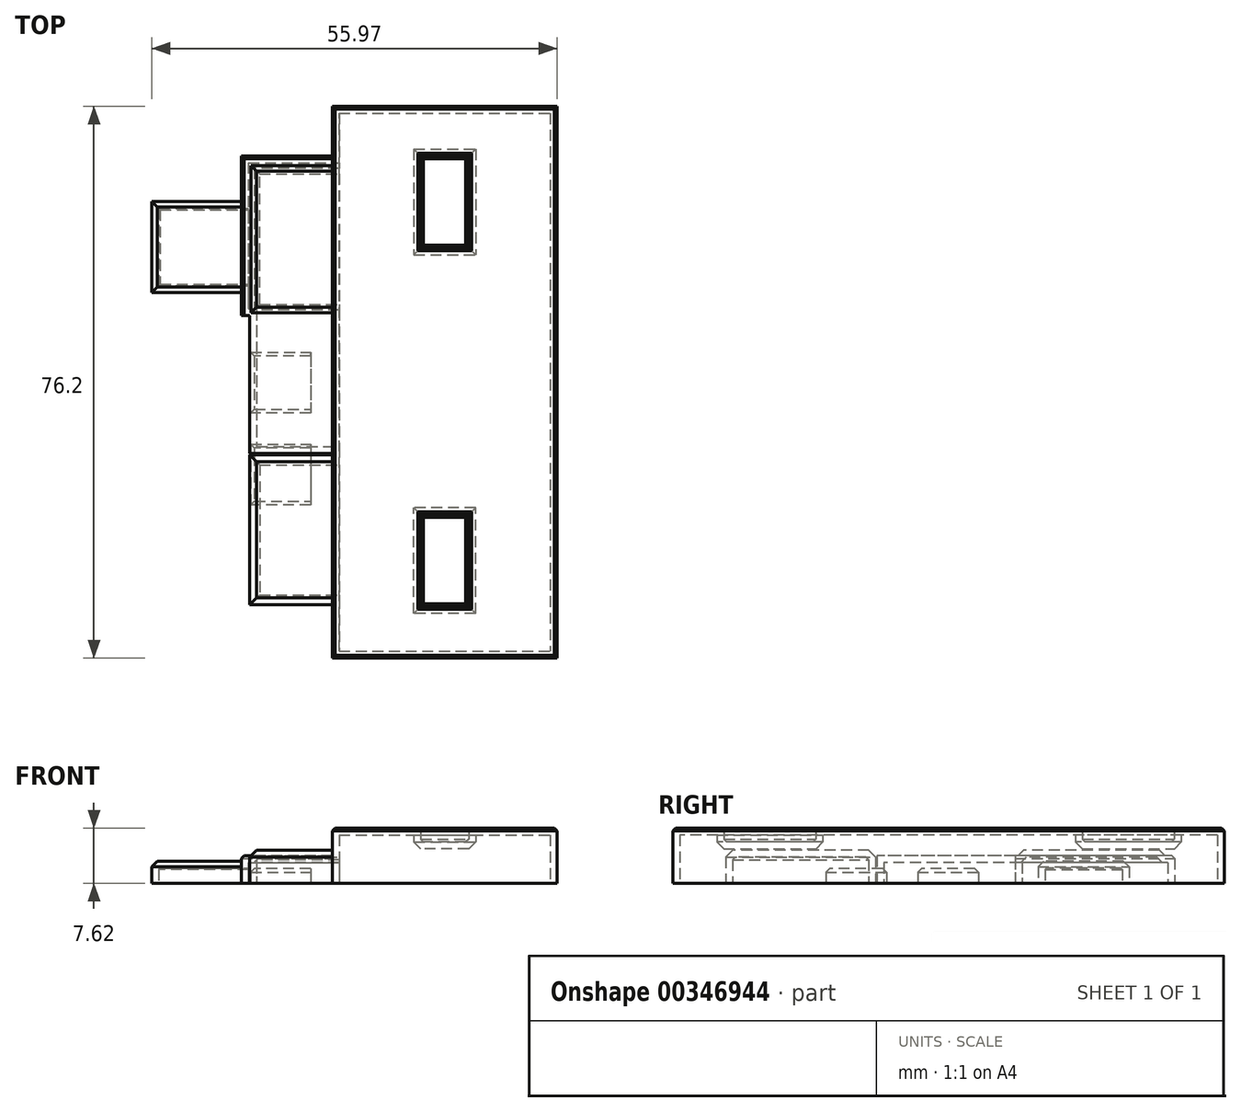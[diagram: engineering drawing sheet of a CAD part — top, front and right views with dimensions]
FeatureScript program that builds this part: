
annotation { "Feature Type Name" : "Feature", "Feature Type Description" : "" }
export const myFeature = defineFeature(function(context is Context, id is Id, definition is map)
    precondition{}
    {
        {
            var Q0;
            Q0=qCreatedBy(makeId("Top.planeOp"),FACE);
            var sketch = newSketch(context, id + "F0", { "sketchPlane" : qUnion([Q0])});
            skLineSegment(sketch, "E0.bottom", {"start": v(-10.71, 25.02) * mm, "end": v(9.98, 25.02) * mm});
            skLineSegment(sketch, "E0.top", {"start": v(-10.71, -25.78) * mm, "end": v(9.98, -25.78) * mm});
            skLineSegment(sketch, "E0.right", {"start": v(9.98, 25.02) * mm, "end": v(9.98, -25.78) * mm});
            skLineSegment(sketch, "E1.bottom", {"start": v(-27.33, 16.25) * mm, "end": v(-19.07, 16.25) * mm});
            skLineSegment(sketch, "E1.top", {"start": v(-27.33, 7.88) * mm, "end": v(-19.07, 7.88) * mm});
            skLineSegment(sketch, "E1.left", {"start": v(-27.33, 16.25) * mm, "end": v(-27.33, 7.88) * mm});
            skLineSegment(sketch, "E1.right", {"start": v(-19.07, 16.25) * mm, "end": v(-19.07, 7.88) * mm});
            skLineSegment(sketch, "E2.bottom", {"start": v(-2.56, 20.43) * mm, "end": v(1.85, 20.43) * mm});
            skLineSegment(sketch, "E2.top", {"start": v(-2.56, 11.96) * mm, "end": v(1.85, 11.96) * mm});
            skLineSegment(sketch, "E2.left", {"start": v(-2.56, 20.43) * mm, "end": v(-2.56, 11.96) * mm});
            skLineSegment(sketch, "E2.right", {"start": v(1.85, 20.43) * mm, "end": v(1.85, 11.96) * mm});
            skLineSegment(sketch, "E3.0.1.0", {"start": v(-2.56, -12.59) * mm, "end": v(1.85, -12.59) * mm});
            skLineSegment(sketch, "E3.0.1.1", {"start": v(-2.56, -12.59) * mm, "end": v(-2.56, -21.06) * mm});
            skLineSegment(sketch, "E3.0.1.2", {"start": v(1.85, -12.59) * mm, "end": v(1.85, -21.06) * mm});
            skLineSegment(sketch, "E3.0.1.3", {"start": v(-2.56, -21.06) * mm, "end": v(1.85, -21.06) * mm});
            skLineSegment(sketch, "E3.direction1", {"start": v(-2.56, 20.43) * mm, "end": v(4.81, 20.43) * mm, "construction": true});
            skLineSegment(sketch, "E3.direction2", {"start": v(-2.56, 20.43) * mm, "end": v(-2.56, -12.59) * mm, "construction": true});
            skLineSegment(sketch, "E4.0.1.0", {"start": v(-19.07, 3.55) * mm, "end": v(-19.07, -4.82) * mm});
            skLineSegment(sketch, "E4.0.1.1", {"start": v(-27.33, 3.55) * mm, "end": v(-19.07, 3.55) * mm});
            skLineSegment(sketch, "E4.0.1.2", {"start": v(-27.33, -4.82) * mm, "end": v(-19.07, -4.82) * mm});
            skLineSegment(sketch, "E4.0.1.3", {"start": v(-27.33, 3.55) * mm, "end": v(-27.33, -4.82) * mm});
            skLineSegment(sketch, "E4.0.2.0", {"start": v(-19.07, -9.15) * mm, "end": v(-19.07, -17.52) * mm});
            skLineSegment(sketch, "E4.0.2.1", {"start": v(-27.33, -9.15) * mm, "end": v(-19.07, -9.15) * mm});
            skLineSegment(sketch, "E4.0.2.2", {"start": v(-27.33, -17.52) * mm, "end": v(-19.07, -17.52) * mm});
            skLineSegment(sketch, "E4.0.2.3", {"start": v(-27.33, -9.15) * mm, "end": v(-27.33, -17.52) * mm});
            skLineSegment(sketch, "E5", {"start": v(-10.71, 25.02) * mm, "end": v(-10.71, -25.78) * mm});
            skLineSegment(sketch, "E6.bottom", {"start": v(-19.07, 20.46) * mm, "end": v(-10.71, 20.46) * mm});
            skLineSegment(sketch, "E6.top", {"start": v(-19.07, 5.76) * mm, "end": v(-10.71, 5.76) * mm});
            skLineSegment(sketch, "E6.left", {"start": v(-19.07, 20.46) * mm, "end": v(-19.07, 5.76) * mm});
            skLineSegment(sketch, "E6.right", {"start": v(-10.71, 20.46) * mm, "end": v(-10.71, 5.76) * mm});
            skLineSegment(sketch, "E7.top", {"start": v(-19.07, -6.96) * mm, "end": v(-10.71, -6.96) * mm});
            skLineSegment(sketch, "E7.left", {"start": v(-19.07, 5.76) * mm, "end": v(-19.07, -6.96) * mm});
            skLineSegment(sketch, "E7.right", {"start": v(-10.71, 5.76) * mm, "end": v(-10.71, -6.96) * mm});
            skLineSegment(sketch, "E8.top", {"start": v(-19.07, -21.65) * mm, "end": v(-10.71, -21.65) * mm});
            skLineSegment(sketch, "E8.left", {"start": v(-19.07, -6.96) * mm, "end": v(-19.07, -21.65) * mm});
            skLineSegment(sketch, "E8.right", {"start": v(-10.71, -6.96) * mm, "end": v(-10.71, -21.65) * mm});
            skLineSegment(sketch, "E9.0", {"start": v(-18.3, 19.7) * mm, "end": v(-10.71, 19.7) * mm});
            skLineSegment(sketch, "E9.2", {"start": v(-18.3, 5.9) * mm, "end": v(-10.71, 5.9) * mm});
            skLineSegment(sketch, "E10.0", {"start": v(-18.3, 5.76) * mm, "end": v(-10.71, 5.76) * mm});
            skLineSegment(sketch, "E10.2", {"start": v(-18.3, -6.96) * mm, "end": v(-10.71, -6.96) * mm});
            skLineSegment(sketch, "E11.MirrorCS", {"start": v(-19.07, -6.96) * mm, "end": v(-19.07, 7.73) * mm});
            skLineSegment(sketch, "E12.0", {"start": v(-18.3, -7.09) * mm, "end": v(-10.71, -7.09) * mm});
            skLineSegment(sketch, "E12.2", {"start": v(-18.3, -20.9) * mm, "end": v(-10.71, -20.9) * mm});
            skLineSegment(sketch, "E13", {"start": v(-18.3, 5.76) * mm, "end": v(-18.3, -6.96) * mm});
            skLineSegment(sketch, "E14", {"start": v(-18.3, -7.09) * mm, "end": v(-18.3, -20.9) * mm});
            skLineSegment(sketch, "E15", {"start": v(-18.3, 5.9) * mm, "end": v(-18.3, 19.7) * mm});
            skSolve(sketch);
        }
        {
            var Q0;
            {var subQ0=sQuery(id+"F0.wireOp",EDGE,"E0.bottom");Q0=makeQuery(id+"F0.imprint","IMPRINT",FACE,{"disambiguationData":[TD([[makeQuery(id+"F0.imprint","IMPRINT",EDGE,{"derivedFrom":subQ0}),-1.0]])]});}
            extrude(context, id + "F1", {"entities" : qUnion([Q0]), "depth" : 5.08 * mm});
        }
        {
            var Q0;
            {var subQ4=sQuery(id+"F0.wireOp",EDGE,"E6.bottom");Q0=makeQuery(id+"F0.imprint","IMPRINT",FACE,{"disambiguationData":[TD([[makeQuery(id+"F0.imprint","IMPRINT",EDGE,{"derivedFrom":subQ4}),-1.0]])]});}
            var Q1;
            {var subQ4=sQuery(id+"F0.wireOp",EDGE,"E6.top");Q1=makeQuery(id+"F0.imprint","IMPRINT",FACE,{"disambiguationData":[TD([[makeQuery(id+"F0.imprint","IMPRINT",EDGE,{"derivedFrom":subQ4}),-1.0]])]});}
            var Q2;
            {var subQ3=sQuery(id+"F0.wireOp",EDGE,"E7.top");Q2=makeQuery(id+"F0.imprint","IMPRINT",FACE,{"disambiguationData":[TD([[makeQuery(id+"F0.imprint","IMPRINT",EDGE,{"derivedFrom":subQ3}),-1.0]])]});}
            extrude(context, id + "F2", {"entities" : qUnion([Q0, Q1, Q2]), "operationType" : NewBodyOperationType.ADD, "depth" : 2.54 * mm});
        }
        {
            var Q0;
            {var subQ0=sQuery(id+"F0.wireOp",EDGE,"E1.bottom");Q0=makeQuery(id+"F0.imprint","IMPRINT",FACE,{"disambiguationData":[TD([[makeQuery(id+"F0.imprint","IMPRINT",EDGE,{"derivedFrom":subQ0}),-1.0]])]});}
            var Q1;
            {var subQ0=sQuery(id+"F0.wireOp",EDGE,"E4.0.1.1");Q1=makeQuery(id+"F0.imprint","IMPRINT",FACE,{"disambiguationData":[TD([[makeQuery(id+"F0.imprint","IMPRINT",EDGE,{"derivedFrom":subQ0}),-1.0]])]});}
            var Q2;
            {var subQ0=sQuery(id+"F0.wireOp",EDGE,"E4.0.2.1");Q2=makeQuery(id+"F0.imprint","IMPRINT",FACE,{"disambiguationData":[TD([[makeQuery(id+"F0.imprint","IMPRINT",EDGE,{"derivedFrom":subQ0}),-1.0]])]});}
            extrude(context, id + "F3", {"entities" : qUnion([Q0, Q1, Q2]), "operationType" : NewBodyOperationType.ADD, "depth" : 2.03 * mm});
        }
        {
            var Q0;
            {var subQ0=sQuery(id+"F0.wireOp",EDGE,"E9.0");Q0=makeQuery(id+"F0.imprint","IMPRINT",FACE,{"disambiguationData":[TD([[makeQuery(id+"F0.imprint","IMPRINT",EDGE,{"derivedFrom":subQ0}),-1.0]])]});}
            var Q1;
            {var subQ0=sQuery(id+"F0.wireOp",EDGE,"E10.0");Q1=makeQuery(id+"F0.imprint","IMPRINT",FACE,{"disambiguationData":[TD([[makeQuery(id+"F0.imprint","IMPRINT",EDGE,{"derivedFrom":subQ0}),-1.0]])]});}
            var Q2;
            {var subQ0=sQuery(id+"F0.wireOp",EDGE,"E12.0");Q2=makeQuery(id+"F0.imprint","IMPRINT",FACE,{"disambiguationData":[TD([[makeQuery(id+"F0.imprint","IMPRINT",EDGE,{"derivedFrom":subQ0}),-1.0]])]});}
            extrude(context, id + "F4", {"entities" : qUnion([Q0, Q1, Q2]), "operationType" : NewBodyOperationType.ADD, "depth" : 3.05 * mm});
        }
        {
            var Q0;
            Q0=makeQuery(id+"F0.imprint","IMPRINT",FACE,{"disambiguationData":[TD([[makeQuery(id+"F0.imprint","IMPRINT",EDGE,{"derivedFrom":sQuery(id+"F0.wireOp",EDGE,"E2.bottom")}),-1.0]])]});
            var Q1;
            Q1=makeQuery(id+"F0.imprint","IMPRINT",FACE,{"disambiguationData":[TD([[makeQuery(id+"F0.imprint","IMPRINT",EDGE,{"derivedFrom":sQuery(id+"F0.wireOp",EDGE,"E3.0.1.0")}),-1.0]])]});
            extrude(context, id + "F5", {"entities" : qUnion([Q0, Q1]), "operationType" : NewBodyOperationType.ADD, "depth" : 3.8 * mm});
        }
        {
            var Q0;
            Q0=makeQuery(id+"F4.opExtrude","CAP_EDGE",EDGE,{"disambiguationData":[OSD([sQuery(id+"F0.wireOp",EDGE,"E9.1")])],"isStart":false});
            var Q1;
            Q1=makeQuery(id+"F4.opExtrude","CAP_EDGE",EDGE,{"disambiguationData":[OSD([sQuery(id+"F0.wireOp",EDGE,"E10.1")])],"isStart":false});
            var Q2;
            Q2=makeQuery(id+"F4.opExtrude","CAP_EDGE",EDGE,{"disambiguationData":[OSD([sQuery(id+"F0.wireOp",EDGE,"E12.1")])],"isStart":false});
            var Q3;
            Q3=makeQuery(id+"F4.opExtrude","CAP_EDGE",EDGE,{"disambiguationData":[OSD([sQuery(id+"F0.wireOp",EDGE,"E12.2")])],"isStart":false});
            var Q4;
            Q4=makeQuery(id+"F4.opExtrude","CAP_EDGE",EDGE,{"disambiguationData":[OSD([sQuery(id+"F0.wireOp",EDGE,"E10.2")])],"isStart":false});
            var Q5;
            Q5=makeQuery(id+"F4.opExtrude","CAP_EDGE",EDGE,{"disambiguationData":[OSD([sQuery(id+"F0.wireOp",EDGE,"E9.2")])],"isStart":false});
            var Q6;
            Q6=makeQuery(id+"F4.opExtrude","CAP_EDGE",EDGE,{"disambiguationData":[OSD([sQuery(id+"F0.wireOp",EDGE,"E9.0")])],"isStart":false});
            var Q7;
            Q7=makeQuery(id+"F4.opExtrude","CAP_EDGE",EDGE,{"disambiguationData":[OSD([sQuery(id+"F0.wireOp",EDGE,"E10.0")])],"isStart":false});
            var Q8;
            Q8=makeQuery(id+"F4.opExtrude","CAP_EDGE",EDGE,{"disambiguationData":[OSD([sQuery(id+"F0.wireOp",EDGE,"E12.0")])],"isStart":false});
            var Q9;
            Q9=makeQuery(id+"F4.opExtrude","CAP_EDGE",EDGE,{"disambiguationData":[OSD([sQuery(id+"F0.wireOp",EDGE,"E13")])],"isStart":false});
            var Q10;
            Q10=makeQuery(id+"F4.opExtrude","CAP_EDGE",EDGE,{"disambiguationData":[OSD([sQuery(id+"F0.wireOp",EDGE,"E15")])],"isStart":false});
            var Q11;
            Q11=makeQuery(id+"F4.opExtrude","CAP_EDGE",EDGE,{"disambiguationData":[OSD([sQuery(id+"F0.wireOp",EDGE,"E14")])],"isStart":false});
            chamfer(context, id + "F6", {"entities" : qUnion([Q0, Q1, Q2, Q3, Q4, Q5, Q6, Q7, Q8, Q9, Q10, Q11]), "width" : 0.64 * mm, "tangentPropagation" : true});
        }
        {
            var Q0;
            Q0=makeQuery(id+"F1.opExtrude","CAP_FACE",FACE,{"disambiguationData":[OSD([sQuery(id+"F0.wireOp",EDGE,"E0.bottom"),sQuery(id+"F0.wireOp",EDGE,"E0.top"),sQuery(id+"F0.wireOp",EDGE,"E0.right"),sQuery(id+"F0.wireOp",EDGE,"E2.bottom"),sQuery(id+"F0.wireOp",EDGE,"E2.top"),sQuery(id+"F0.wireOp",EDGE,"E2.left"),sQuery(id+"F0.wireOp",EDGE,"E2.right"),sQuery(id+"F0.wireOp",EDGE,"E3.0.1.0"),sQuery(id+"F0.wireOp",EDGE,"E3.0.1.1"),sQuery(id+"F0.wireOp",EDGE,"E3.0.1.2"),sQuery(id+"F0.wireOp",EDGE,"E3.0.1.3"),sQuery(id+"F0.wireOp",EDGE,"E5"),sQuery(id+"F0.wireOp",EDGE,"E6.right"),sQuery(id+"F0.wireOp",EDGE,"E7.right"),sQuery(id+"F0.wireOp",EDGE,"E8.right")])],"isStart":false});
            chamfer(context, id + "F7", {"entities" : qUnion([Q0]), "width" : 0.25 * mm, "tangentPropagation" : true});
        }
        {
            var Q0;
            Q0=makeQuery(id+"F5.opExtrude","CAP_FACE",FACE,{"disambiguationData":[OSD([sQuery(id+"F0.wireOp",EDGE,"E2.bottom"),sQuery(id+"F0.wireOp",EDGE,"E2.top"),sQuery(id+"F0.wireOp",EDGE,"E2.left"),sQuery(id+"F0.wireOp",EDGE,"E2.right")])],"isStart":false});
            var Q1;
            Q1=makeQuery(id+"F5.opExtrude","CAP_FACE",FACE,{"disambiguationData":[OSD([sQuery(id+"F0.wireOp",EDGE,"E3.0.1.0"),sQuery(id+"F0.wireOp",EDGE,"E3.0.1.1"),sQuery(id+"F0.wireOp",EDGE,"E3.0.1.2"),sQuery(id+"F0.wireOp",EDGE,"E3.0.1.3")])],"isStart":false});
            chamfer(context, id + "F8", {"entities" : qUnion([Q0, Q1]), "width" : 0.25 * mm, "tangentPropagation" : true});
        }
        {
            var Q0;
            Q0=makeQuery(id+"F2.opExtrude","CAP_EDGE",EDGE,{"disambiguationData":[OSD([sQuery(id+"F0.wireOp",EDGE,"E6.left"),sQuery(id+"F0.wireOp",EDGE,"E8.left"),sQuery(id+"F0.wireOp",EDGE,"E11.MirrorCS")])],"isStart":false});
            var Q1;
            Q1=makeQuery(id+"F2.opExtrude","CAP_EDGE",EDGE,{"disambiguationData":[OSD([sQuery(id+"F0.wireOp",EDGE,"E6.bottom")])],"isStart":false});
            var Q2;
            Q2=makeQuery(id+"F2.opExtrude","CAP_EDGE",EDGE,{"disambiguationData":[OSD([sQuery(id+"F0.wireOp",EDGE,"E8.top")])],"isStart":false});
            chamfer(context, id + "F9", {"entities" : qUnion([Q0, Q1, Q2]), "width" : 0.25 * mm, "tangentPropagation" : true});
        }
        {
            var Q0;
            Q0=makeQuery(id+"F3.opExtrude","CAP_EDGE",EDGE,{"disambiguationData":[OSD([sQuery(id+"F0.wireOp",EDGE,"E1.left")])],"isStart":false});
            var Q1;
            Q1=makeQuery(id+"F3.opExtrude","CAP_EDGE",EDGE,{"disambiguationData":[OSD([sQuery(id+"F0.wireOp",EDGE,"E1.top")])],"isStart":false});
            var Q2;
            Q2=makeQuery(id+"F3.opExtrude","CAP_EDGE",EDGE,{"disambiguationData":[OSD([sQuery(id+"F0.wireOp",EDGE,"E1.bottom")])],"isStart":false});
            var Q3;
            Q3=makeQuery(id+"F3.opExtrude","CAP_EDGE",EDGE,{"disambiguationData":[OSD([sQuery(id+"F0.wireOp",EDGE,"E4.0.1.1")])],"isStart":false});
            var Q4;
            Q4=makeQuery(id+"F3.opExtrude","CAP_EDGE",EDGE,{"disambiguationData":[OSD([sQuery(id+"F0.wireOp",EDGE,"E4.0.1.3")])],"isStart":false});
            var Q5;
            Q5=makeQuery(id+"F3.opExtrude","CAP_EDGE",EDGE,{"disambiguationData":[OSD([sQuery(id+"F0.wireOp",EDGE,"E4.0.1.2")])],"isStart":false});
            var Q6;
            Q6=makeQuery(id+"F3.opExtrude","CAP_EDGE",EDGE,{"disambiguationData":[OSD([sQuery(id+"F0.wireOp",EDGE,"E4.0.2.1")])],"isStart":false});
            var Q7;
            Q7=makeQuery(id+"F3.opExtrude","CAP_EDGE",EDGE,{"disambiguationData":[OSD([sQuery(id+"F0.wireOp",EDGE,"E4.0.2.3")])],"isStart":false});
            var Q8;
            Q8=makeQuery(id+"F3.opExtrude","CAP_EDGE",EDGE,{"disambiguationData":[OSD([sQuery(id+"F0.wireOp",EDGE,"E4.0.2.2")])],"isStart":false});
            chamfer(context, id + "F10", {"entities" : qUnion([Q0, Q1, Q2, Q3, Q4, Q5, Q6, Q7, Q8]), "width" : 0.5 * mm, "tangentPropagation" : true});
        }
        {
            var Q0;
            {var subQ0=sQuery(id+"F0.wireOp",EDGE,"E3.0.1.3");var subQ1=sQuery(id+"F0.wireOp",EDGE,"E3.0.1.2");var subQ2=sQuery(id+"F0.wireOp",EDGE,"E3.0.1.1");var subQ3=sQuery(id+"F0.wireOp",EDGE,"E3.0.1.0");var subQ4=sQuery(id+"F0.wireOp",EDGE,"E2.right");var subQ5=sQuery(id+"F0.wireOp",EDGE,"E2.left");var subQ6=sQuery(id+"F0.wireOp",EDGE,"E2.top");var subQ7=sQuery(id+"F0.wireOp",EDGE,"E2.bottom");var subQ8=sQuery(id+"F0.wireOp",EDGE,"E7.right");var subQ9=sQuery(id+"F0.wireOp",EDGE,"E13");var subQ10=sQuery(id+"F0.wireOp",EDGE,"E10.2");var subQ11=sQuery(id+"F0.wireOp",EDGE,"E10.0");var subQ12=sQuery(id+"F0.wireOp",EDGE,"E14");var subQ13=sQuery(id+"F0.wireOp",EDGE,"E12.2");var subQ14=sQuery(id+"F0.wireOp",EDGE,"E12.0");var subQ15=sQuery(id+"F0.wireOp",EDGE,"E8.right");var subQ16=sQuery(id+"F0.wireOp",EDGE,"E15");var subQ17=sQuery(id+"F0.wireOp",EDGE,"E9.2");var subQ18=sQuery(id+"F0.wireOp",EDGE,"E9.0");var subQ19=sQuery(id+"F0.wireOp",EDGE,"E6.right");var subQ20=sQuery(id+"F0.wireOp",EDGE,"E8.left");var subQ21=sQuery(id+"F0.wireOp",EDGE,"E11.MirrorCS");var subQ22=sQuery(id+"F0.wireOp",EDGE,"E6.left");Q0=makeQuery(id+"F5.boolean.opBoolean","MERGE",FACE,{"derivedFrom":[makeQuery(id+"F4.boolean.opBoolean","MERGE",FACE,{"derivedFrom":[makeQuery(id+"F3.boolean.opBoolean","MERGE",FACE,{"derivedFrom":[makeQuery(id+"F2.boolean.opBoolean","MERGE",FACE,{"derivedFrom":[makeQuery(id+"F1.opExtrude","CAP_FACE",FACE,{"disambiguationData":[OSD([sQuery(id+"F0.wireOp",EDGE,"E0.bottom"),sQuery(id+"F0.wireOp",EDGE,"E0.top"),sQuery(id+"F0.wireOp",EDGE,"E0.right"),subQ7,subQ6,subQ5,subQ4,subQ3,subQ2,subQ1,subQ0,sQuery(id+"F0.wireOp",EDGE,"E5"),subQ19,subQ15,subQ8])],"isStart":true}),makeQuery(id+"F2.opExtrude","CAP_FACE",FACE,{"disambiguationData":[OSD([sQuery(id+"F0.wireOp",EDGE,"E6.bottom"),subQ22,subQ19,sQuery(id+"F0.wireOp",EDGE,"E8.top"),subQ20,subQ15,subQ18,subQ17,subQ11,subQ10,subQ21,subQ14,subQ13,subQ9,subQ12,subQ16])],"isStart":true})]}),makeQuery(id+"F3.opExtrude","CAP_FACE",FACE,{"disambiguationData":[OSD([sQuery(id+"F0.wireOp",EDGE,"E1.bottom"),sQuery(id+"F0.wireOp",EDGE,"E1.top"),sQuery(id+"F0.wireOp",EDGE,"E1.left"),subQ22])],"isStart":true}),makeQuery(id+"F3.opExtrude","CAP_FACE",FACE,{"disambiguationData":[OSD([sQuery(id+"F0.wireOp",EDGE,"E4.0.1.1"),sQuery(id+"F0.wireOp",EDGE,"E4.0.1.2"),sQuery(id+"F0.wireOp",EDGE,"E4.0.1.3"),subQ21])],"isStart":true}),makeQuery(id+"F3.opExtrude","CAP_FACE",FACE,{"disambiguationData":[OSD([sQuery(id+"F0.wireOp",EDGE,"E4.0.2.1"),sQuery(id+"F0.wireOp",EDGE,"E4.0.2.2"),sQuery(id+"F0.wireOp",EDGE,"E4.0.2.3"),subQ20])],"isStart":true})]}),makeQuery(id+"F4.opExtrude","CAP_FACE",FACE,{"disambiguationData":[OSD([subQ19,subQ18,subQ17,subQ16])],"isStart":true}),makeQuery(id+"F4.opExtrude","CAP_FACE",FACE,{"disambiguationData":[OSD([subQ15,subQ14,subQ13,subQ12])],"isStart":true}),makeQuery(id+"F4.opExtrude","CAP_FACE",FACE,{"disambiguationData":[OSD([subQ11,subQ10,subQ9,subQ8])],"isStart":true})]}),makeQuery(id+"F5.opExtrude","CAP_FACE",FACE,{"disambiguationData":[OSD([subQ7,subQ6,subQ5,subQ4])],"isStart":true}),makeQuery(id+"F5.opExtrude","CAP_FACE",FACE,{"disambiguationData":[OSD([subQ3,subQ2,subQ1,subQ0])],"isStart":true})]});}
            shell(context, id + "F11", {"entities" : qUnion([Q0]), "thickness" : 0.64 * mm});
        }
        {
            var Q0;
            Q0=makeQuery(id+"F1.opExtrude","SWEPT_BODY",BODY,{"disambiguationData":[OSD([sQuery(id+"F0.wireOp",EDGE,"E0.bottom"),sQuery(id+"F0.wireOp",EDGE,"E0.top"),sQuery(id+"F0.wireOp",EDGE,"E0.right"),sQuery(id+"F0.wireOp",EDGE,"E2.bottom"),sQuery(id+"F0.wireOp",EDGE,"E2.top"),sQuery(id+"F0.wireOp",EDGE,"E2.left"),sQuery(id+"F0.wireOp",EDGE,"E2.right"),sQuery(id+"F0.wireOp",EDGE,"E3.0.1.0"),sQuery(id+"F0.wireOp",EDGE,"E3.0.1.1"),sQuery(id+"F0.wireOp",EDGE,"E3.0.1.2"),sQuery(id+"F0.wireOp",EDGE,"E3.0.1.3"),sQuery(id+"F0.wireOp",EDGE,"E5"),sQuery(id+"F0.wireOp",EDGE,"E6.right"),sQuery(id+"F0.wireOp",EDGE,"E8.right"),sQuery(id+"F0.wireOp",EDGE,"E7.right")])]});
            var Q1;
            Q1=qCreatedBy(makeId("Origin.pointOp"),VERTEX);
            transform(context, id + "F12", {"entities" : qUnion([Q0]), "transformType" : TransformType.SCALE_UNIFORMLY, "scale" : 1.5, "scalePoint" : qUnion([Q1]), "makeCopy" : false});
        }
    });
